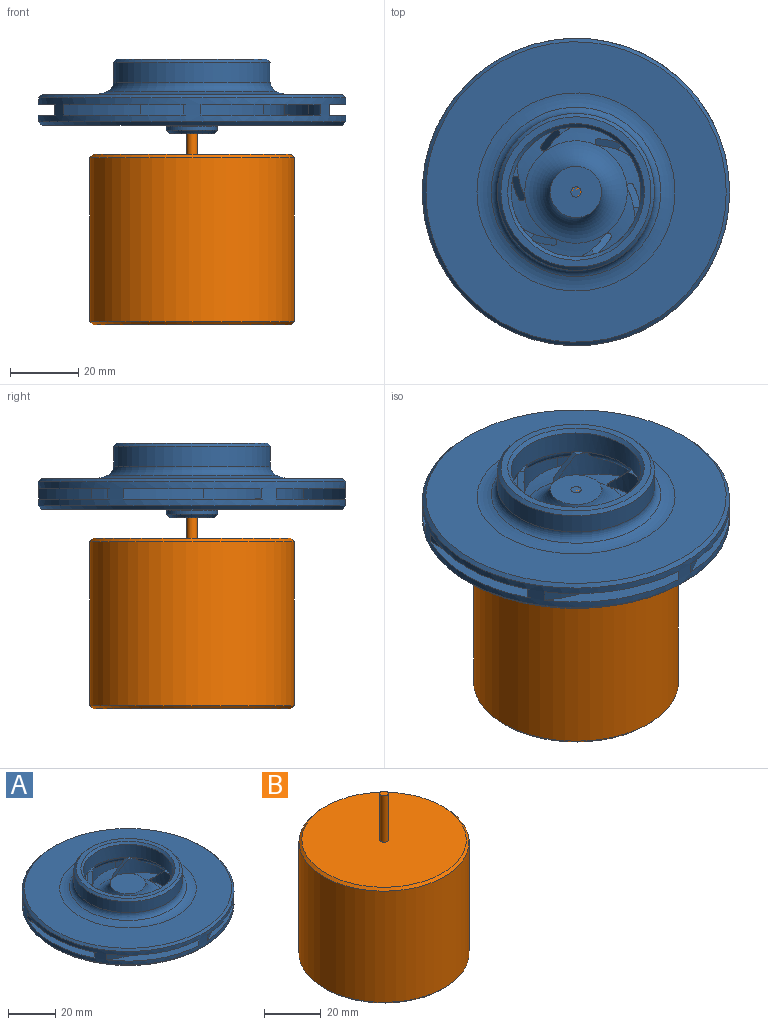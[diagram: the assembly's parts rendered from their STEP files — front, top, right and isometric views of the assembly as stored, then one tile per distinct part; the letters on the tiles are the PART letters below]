
ASSEMBLY  parts=2 mates=1
PART A: 104 faces, bbox 90.1x90.1x22 mm
  f0: plane 58.21x35.73mm, normal (0,0,1), area 534.2mm2, adj f7,f20,f52,f55,f60,f64
  f1: plane 61.99x29.25mm, normal (0,0,1), area 534.2mm2, adj f5,f20,f62,f65,f98,f101
  f2: plane 50.96x43.62mm, normal (0,0,1), area 534.2mm2, adj f6,f20,f53,f56,f70,f73
  f3: plane 61.99x29.25mm, normal (0,0,1), area 534.2mm2, adj f8,f20,f71,f74,f79,f82
  f4: plane 58.21x35.73mm, normal (0,0,1), area 534.2mm2, adj f9,f20,f80,f83,f88,f91
  f5: torus R=29mm, axis (0,0,1), area 246mm2, adj f1,f12,f59,f61,f62,f95,f96,f98
  f6: torus R=29mm, axis (0,0,1), area 246mm2, adj f2,f12,f50,f51,f53,f67,f69,f70
  f7: torus R=29mm, axis (0,0,1), area 246mm2, adj f0,f12,f49,f51,f52,f58,f60,f61
  f8: torus R=29mm, axis (0,0,1), area 246mm2, adj f3,f12,f68,f69,f71,f76,f78,f79
  f9: torus R=29mm, axis (0,0,1), area 246mm2, adj f4,f12,f77,f78,f80,f85,f87,f88
  f10: torus R=29mm, axis (0,0,1), area 246mm2, adj f11,f12,f86,f87,f89,f94,f96,f97
  f11: plane 50.96x43.62mm, normal (0,0,1), area 534.2mm2, adj f10,f20,f89,f92,f97,f100
  f12: torus R=17.12mm, axis (0,0,1), area 718mm2, adj f5,f6,f7,f8,f9,f10,f13
  f13: plane 15x15mm, normal (0,0,1), area 176.7mm2, adj f12
  f14: plane 13x13mm, normal (0,0,-1), area 132.7mm2, adj f103
  f15: cylinder r=7.5mm len=15mm, axis (0,0,1), area 56.8mm2, adj f16,f103
  f16: torus R=10.5mm, axis (0,0,1), area 343.8mm2, adj f15,f17
  f17: torus R=17.12mm, axis (0,0,1), area 226.9mm2, adj f16,f18
  f18: torus R=29mm, axis (0,0,1), area 2006.5mm2, adj f17,f19
  f19: plane 88x88mm, normal (0,0,-1), area 3440mm2, adj f18,f21
  f20: cylinder r=45mm len=90mm, axis (0,0,1), area 1225.1mm2, adj f0,f1,f2,f3,f4,f11,f21,f26
  f21: cone r=45mm half-angle=45deg, axis (0,0,1), area 395.4mm2, adj f19,f20
  f22: torus R=22mm, axis (0,0,1), area 38.9mm2, adj f25,f42,f59,f95,f99
  f23: torus R=22mm, axis (0,0,1), area 38.9mm2, adj f24,f42,f86,f90,f94
  f24: torus R=29mm, axis (0,0,1), area 189.1mm2, adj f23,f26,f86,f89,f94,f97
  f25: torus R=29mm, axis (0,0,1), area 189.1mm2, adj f22,f43,f59,f62,f95,f98
  f26: plane 50.96x43.62mm, normal (0,0,-1), area 534.2mm2, adj f20,f24,f89,f92,f97,f100
  f27: torus R=22mm, axis (0,0,1), area 38.9mm2, adj f28,f42,f77,f81,f85
  f28: torus R=29mm, axis (0,0,1), area 189.1mm2, adj f27,f29,f77,f80,f85,f88
  f29: plane 58.21x35.73mm, normal (0,0,-1), area 534.2mm2, adj f20,f28,f80,f83,f88,f91
  f30: torus R=22mm, axis (0,0,1), area 38.9mm2, adj f31,f42,f68,f72,f76
  f31: torus R=29mm, axis (0,0,1), area 189.1mm2, adj f30,f32,f68,f71,f76,f79
  f32: plane 61.99x29.25mm, normal (0,0,-1), area 534.2mm2, adj f20,f31,f71,f74,f79,f82
  f33: torus R=22mm, axis (0,0,1), area 38.9mm2, adj f34,f42,f50,f54,f67
  f34: torus R=29mm, axis (0,0,1), area 189.1mm2, adj f33,f35,f50,f53,f67,f70
  f35: plane 50.96x43.62mm, normal (0,0,-1), area 534.2mm2, adj f20,f34,f53,f56,f70,f73
  f36: torus R=22mm, axis (0,0,1), area 38.9mm2, adj f37,f42,f49,f58,f63
  f37: torus R=29mm, axis (0,0,1), area 189.1mm2, adj f36,f38,f49,f52,f58,f60
  f38: plane 58.21x35.73mm, normal (0,0,-1), area 534.2mm2, adj f20,f37,f52,f55,f60,f64
  f39: torus R=26mm, axis (0,0,1), area 519.4mm2, adj f40,f45
  f40: cylinder r=23mm len=46mm, axis (0,0,1), area 835.7mm2, adj f39,f47
  f41: plane 44x44mm, normal (0,0,1), area 263.9mm2, adj f47,f48
  f42: cylinder r=19mm len=38mm, axis (0,0,1), area 807.5mm2, adj f22,f23,f27,f30,f33,f36,f48,f57
  f43: plane 61.99x29.25mm, normal (0,0,-1), area 534.2mm2, adj f20,f25,f62,f65,f98,f101
  f44: plane 88x88mm, normal (0,0,1), area 3440mm2, adj f45,f46
  f45: torus R=29mm, axis (0,0,1), area 726mm2, adj f39,f44
  f46: cone r=44mm half-angle=45deg, axis (0,0,-1), area 395.4mm2, adj f20,f44
  f47: cone r=22mm half-angle=45deg, axis (0,0,-1), area 199.9mm2, adj f40,f41
  f48: cone r=19mm half-angle=45deg, axis (0,0,1), area 173.3mm2, adj f41,f42
  f49: cylinder r=19mm len=21.17mm, axis (0,0,1), area 126.5mm2, adj f7,f36,f37,f51,f52,f54,f57
  f50: cylinder r=21mm len=23.4mm, axis (0,0,1), area 116.1mm2, adj f6,f33,f34,f51,f53,f54
  f51: cylinder r=1mm len=1.84mm, axis (0,0,1), area 1.5mm2, adj f6,f7,f49,f50,f54
  f52: cylinder r=34mm len=21.3mm, axis (0,0,1), area 89.6mm2, adj f0,f7,f37,f38,f49,f55
  f53: cylinder r=36mm len=22.55mm, axis (0,0,1), area 92.5mm2, adj f2,f6,f34,f35,f50,f56
  f54: plane 7.34x6.34mm, normal (0.58,0.4,0.71), area 20.1mm2, adj f33,f49,f50,f51,f57
  f55: cylinder r=44mm len=27.23mm, axis (0,0,1), area 83.8mm2, adj f0,f20,f38,f52
  f56: cylinder r=46mm len=23.57mm, axis (0,0,1), area 72.8mm2, adj f2,f20,f35,f53
  f57: plane 3.97x2.02mm, normal (0,0,1), area 3mm2, adj f42,f49,f54
  f58: cylinder r=21mm len=19.33mm, axis (0,0,1), area 116.1mm2, adj f7,f36,f37,f60,f61,f63
  f59: cylinder r=19mm len=17.49mm, axis (0,0,1), area 126.5mm2, adj f5,f22,f25,f61,f62,f63,f66
  f60: cylinder r=36mm len=29.01mm, axis (0,0,1), area 92.5mm2, adj f0,f7,f37,f38,f58,f64
  f61: cylinder r=1mm len=2mm, axis (0,0,1), area 1.5mm2, adj f5,f7,f58,f59,f63
  f62: cylinder r=34mm len=27.4mm, axis (0,0,1), area 89.6mm2, adj f1,f5,f25,f43,f59,f65
  f63: plane 7.61x7.34mm, normal (0.64,-0.3,0.71), area 20.1mm2, adj f36,f58,f59,f61,f66
  f64: cylinder r=46mm len=18.19mm, axis (0,0,1), area 72.8mm2, adj f0,f20,f38,f60
  f65: cylinder r=44mm len=21.76mm, axis (0,0,1), area 83.8mm2, adj f1,f20,f43,f62
  f66: plane 3.29x3.08mm, normal (0,0,1), area 3mm2, adj f42,f59,f63
  f67: cylinder r=19mm len=22.32mm, axis (0,0,1), area 126.5mm2, adj f6,f33,f34,f69,f70,f72,f75
  f68: cylinder r=21mm len=24.67mm, axis (0,0,1), area 116.1mm2, adj f8,f30,f31,f69,f71,f72
  f69: cylinder r=1mm len=1.89mm, axis (0,0,1), area 1.5mm2, adj f6,f8,f67,f68,f72
  f70: cylinder r=34mm len=26.16mm, axis (0,0,1), area 89.6mm2, adj f2,f6,f34,f35,f67,f73
  f71: cylinder r=36mm len=27.7mm, axis (0,0,1), area 92.5mm2, adj f3,f8,f31,f32,f68,f74
  f72: plane 7.34x7.28mm, normal (-0.06,0.7,0.71), area 20.1mm2, adj f30,f67,f68,f69,f75
  f73: cylinder r=44mm len=25.39mm, axis (0,0,1), area 83.8mm2, adj f2,f20,f35,f70
  f74: cylinder r=46mm len=22.63mm, axis (0,0,1), area 72.8mm2, adj f3,f20,f32,f71
  f75: plane 3.8x1.58mm, normal (0,0,1), area 3mm2, adj f42,f67,f72
  f76: cylinder r=19mm len=17.49mm, axis (0,0,1), area 126.5mm2, adj f8,f30,f31,f78,f79,f81,f84
  f77: cylinder r=21mm len=19.33mm, axis (0,0,1), area 116.1mm2, adj f9,f27,f28,f78,f80,f81
  f78: cylinder r=1mm len=2mm, axis (0,0,1), area 1.5mm2, adj f8,f9,f76,f77,f81
  f79: cylinder r=34mm len=27.4mm, axis (0,0,1), area 89.6mm2, adj f3,f8,f31,f32,f76,f82
  f80: cylinder r=36mm len=29.01mm, axis (0,0,1), area 92.5mm2, adj f4,f9,f28,f29,f77,f83
  f81: plane 7.61x7.34mm, normal (-0.64,0.3,0.71), area 20.1mm2, adj f27,f76,f77,f78,f84
  f82: cylinder r=44mm len=21.76mm, axis (0,0,1), area 83.8mm2, adj f3,f20,f32,f79
  f83: cylinder r=46mm len=18.19mm, axis (0,0,1), area 72.8mm2, adj f4,f20,f29,f80
  f84: plane 3.29x3.08mm, normal (0,0,1), area 3mm2, adj f42,f76,f81
  f85: cylinder r=19mm len=21.17mm, axis (0,0,1), area 126.5mm2, adj f9,f27,f28,f87,f88,f90,f93
  f86: cylinder r=21mm len=23.4mm, axis (0,0,1), area 116.1mm2, adj f10,f23,f24,f87,f89,f90
  f87: cylinder r=1mm len=1.84mm, axis (0,0,1), area 1.5mm2, adj f9,f10,f85,f86,f90
  f88: cylinder r=34mm len=21.3mm, axis (0,0,1), area 89.6mm2, adj f4,f9,f28,f29,f85,f91
  f89: cylinder r=36mm len=22.55mm, axis (0,0,1), area 92.5mm2, adj f10,f11,f24,f26,f86,f92
  f90: plane 7.34x6.34mm, normal (-0.58,-0.4,0.71), area 20.1mm2, adj f23,f85,f86,f87,f93
  f91: cylinder r=44mm len=27.23mm, axis (0,0,1), area 83.8mm2, adj f4,f20,f29,f88
  f92: cylinder r=46mm len=23.57mm, axis (0,0,1), area 72.8mm2, adj f11,f20,f26,f89
  f93: plane 3.97x2.02mm, normal (0,0,1), area 3mm2, adj f42,f85,f90
  f94: cylinder r=19mm len=22.32mm, axis (0,0,1), area 126.5mm2, adj f10,f23,f24,f96,f97,f99,f102
  f95: cylinder r=21mm len=24.67mm, axis (0,0,1), area 116.1mm2, adj f5,f22,f25,f96,f98,f99
  f96: cylinder r=1mm len=1.89mm, axis (0,0,1), area 1.5mm2, adj f5,f10,f94,f95,f99
  f97: cylinder r=34mm len=26.16mm, axis (0,0,1), area 89.6mm2, adj f10,f11,f24,f26,f94,f100
  f98: cylinder r=36mm len=27.7mm, axis (0,0,1), area 92.5mm2, adj f1,f5,f25,f43,f95,f101
  f99: plane 7.34x7.28mm, normal (0.06,-0.7,0.71), area 20.1mm2, adj f22,f94,f95,f96,f102
  f100: cylinder r=44mm len=25.39mm, axis (0,0,1), area 83.8mm2, adj f11,f20,f26,f97
  f101: cylinder r=46mm len=22.63mm, axis (0,0,1), area 72.8mm2, adj f1,f20,f43,f98
  f102: plane 3.8x1.58mm, normal (0,0,1), area 3mm2, adj f42,f94,f99
  f103: cone r=7.5mm half-angle=45deg, axis (0,0,1), area 62.2mm2, adj f14,f15
PART B: 318 faces, bbox 60x60x70 mm
  f0: plane 58x58mm, normal (0,0,-1), area 2389.9mm2, adj f5,f7,f8,f9,f10,f11,f12,f13
  f1: cylinder r=30mm len=60mm, axis (0,0,1), area 9047.8mm2, adj f5,f6
  f2: plane 58x58mm, normal (0,0,1), area 2635mm2, adj f3,f6
  f3: cylinder r=1.5mm len=20mm, axis (0,0,1), area 188.5mm2, adj f2,f4
  f4: plane 3x3mm, normal (0,0,1), area 7.1mm2, adj f3
  f5: cone r=30mm half-angle=45deg, axis (0,0,1), area 262.1mm2, adj f0,f1
  f6: cone r=29mm half-angle=45deg, axis (0,0,-1), area 262.1mm2, adj f1,f2
  f7: plane 1x0.85mm, normal (1,-0.05,0), area 0.9mm2, adj f0,f8,f28,f29
  f8: extruded ~1x0.79mm, area 0.8mm2, adj f0,f7,f9,f29
  f9: extruded ~2.7x1mm, area 2.7mm2, adj f0,f8,f10,f29
  f10: extruded ~3.41x2.78mm, area 4.4mm2, adj f0,f9,f11,f29
  f11: extruded ~1.77x1mm, area 1.8mm2, adj f0,f10,f12,f29
  f12: plane 1x0.79mm, normal (1,-0.09,0), area 0.8mm2, adj f0,f11,f13,f29
  f13: extruded ~3.71x1mm, area 3.7mm2, adj f0,f12,f14,f29
  f14: extruded ~1.94x1.2mm, area 2.4mm2, adj f0,f13,f15,f29
  f15: extruded ~3.9x2.28mm, area 5.1mm2, adj f0,f14,f16,f29
  f16: plane 1x0.84mm, normal (-0.98,-0.2,0), area 0.9mm2, adj f0,f15,f17,f29
  f17: extruded ~1.48x1mm, area 1.5mm2, adj f0,f16,f18,f29
  f18: extruded ~1.77x1.51mm, area 2.6mm2, adj f0,f17,f19,f29
  f19: extruded ~1.98x1.95mm, area 3mm2, adj f0,f18,f20,f29
  f20: extruded ~2.61x1mm, area 2.6mm2, adj f0,f19,f21,f29
  f21: plane 1x0.78mm, normal (-1,0,0), area 0.8mm2, adj f0,f20,f22,f29
  f22: extruded ~4.9x1mm, area 4.9mm2, adj f0,f21,f23,f29
  f23: extruded ~3.08x2.53mm, area 4mm2, adj f0,f22,f24,f29
  f24: extruded ~1x0.55mm, area 0.7mm2, adj f0,f23,f25,f29
  f25: plane 1x0.6mm, normal (-0.75,0.66,0), area 0.8mm2, adj f0,f24,f26,f29
  f26: extruded ~1x0.56mm, area 0.6mm2, adj f0,f25,f27,f29
  f27: extruded ~3.17x1mm, area 3.2mm2, adj f0,f26,f28,f29
  f28: extruded ~1x0.82mm, area 0.8mm2, adj f0,f7,f27,f29
  f29: plane 8.49x7.99mm, normal (0,0,-1), area 18.1mm2, adj f7,f8,f9,f10,f11,f12,f13,f14
  f30: extruded ~1x0.69mm, area 0.9mm2, adj f0,f31,f40,f41
  f31: extruded ~3.03x2.59mm, area 4mm2, adj f0,f30,f32,f41
  f32: extruded ~2.06x1mm, area 2.6mm2, adj f0,f31,f33,f41
  f33: extruded ~3.25x2.86mm, area 4.3mm2, adj f0,f32,f34,f41
  f34: extruded ~1x0.75mm, area 1mm2, adj f0,f33,f35,f41
  f35: plane 1x0.75mm, normal (-0.67,-0.74,0), area 1mm2, adj f0,f34,f36,f41
  f36: extruded ~3.85x3.33mm, area 5.1mm2, adj f0,f35,f37,f41
  f37: extruded ~1.25x1mm, area 1.6mm2, adj f0,f36,f38,f41
  f38: extruded ~2.96x2.43mm, area 3.8mm2, adj f0,f37,f39,f41
  f39: extruded ~1x0.71mm, area 0.9mm2, adj f0,f38,f40,f41
  f40: plane 1x0.78mm, normal (-0.66,0.75,0), area 1mm2, adj f0,f30,f39,f41
  f41: plane 8.96x5.52mm, normal (0,0,-1), area 10.7mm2, adj f30,f31,f32,f33,f34,f35,f36,f37
  f42: plane 1x0.76mm, normal (0,-1,0), area 0.8mm2, adj f0,f43,f73,f76
  f43: plane 2.48x1mm, normal (-1,0,0), area 2.5mm2, adj f0,f42,f44,f76
  f44: extruded ~2.47x2.15mm, area 3.3mm2, adj f0,f43,f45,f76
  f45: extruded ~1x0.6mm, area 0.8mm2, adj f0,f44,f46,f76
  f46: extruded ~2.66x2.07mm, area 3.4mm2, adj f0,f45,f47,f76
  f47: plane 2.12x1mm, normal (0,-1,0), area 2.1mm2, adj f0,f46,f48,f76
  f48: plane 2.56x1mm, normal (-1,0,0), area 2.6mm2, adj f0,f47,f49,f76
  f49: plane 2.47x1mm, normal (0,1,0), area 2.5mm2, adj f0,f48,f50,f76
  f50: plane 1x0.87mm, normal (-1,0,0), area 0.9mm2, adj f0,f49,f51,f76
  f51: plane 2.94x1mm, normal (0,-1,0), area 2.9mm2, adj f0,f50,f52,f76
  f52: plane 1x0.67mm, normal (-1,0,0), area 0.7mm2, adj f0,f51,f53,f76
  f53: plane 2.94x1mm, normal (0,1,0), area 2.9mm2, adj f0,f52,f54,f76
  f54: plane 1.06x1mm, normal (-1,0,0), area 1.1mm2, adj f0,f53,f55,f76
  f55: plane 1x0.76mm, normal (0,1,0), area 0.8mm2, adj f0,f54,f56,f76
  f56: plane 1.06x1mm, normal (1,0,0), area 1.1mm2, adj f0,f55,f57,f76
  f57: plane 2.77x1mm, normal (0,1,0), area 2.8mm2, adj f0,f56,f58,f76
  f58: plane 1x0.67mm, normal (1,0,0), area 0.7mm2, adj f0,f57,f59,f76
  f59: plane 2.77x1mm, normal (0,-1,0), area 2.8mm2, adj f0,f58,f60,f76
  f60: plane 1x0.87mm, normal (1,0,0), area 0.9mm2, adj f0,f59,f61,f76
  f61: plane 2.34x1mm, normal (0,1,0), area 2.3mm2, adj f0,f60,f62,f76
  f62: plane 2.56x1mm, normal (1,0,0), area 2.6mm2, adj f0,f61,f63,f76
  f63: plane 1.94x1mm, normal (0,-1,0), area 1.9mm2, adj f0,f62,f64,f76
  f64: extruded ~2.56x2.11mm, area 3.4mm2, adj f0,f63,f65,f76
  f65: extruded ~1x0.58mm, area 0.8mm2, adj f0,f64,f66,f76
  f66: extruded ~2.47x2.21mm, area 3.3mm2, adj f0,f65,f73,f76
  f67: plane 1.63x1mm, normal (0,-1,0), area 1.6mm2, adj f68,f74,f76,f77
  f68: plane 1.32x1mm, normal (1,0,0), area 1.3mm2, adj f67,f69,f76,f77
  f69: plane 1.63x1mm, normal (0,1,0), area 1.6mm2, adj f68,f74,f76,f77
  f70: plane 1.32x1mm, normal (1,0,0), area 1.3mm2, adj f71,f75,f76,f314
  f71: plane 1.72x1mm, normal (0,1,0), area 1.7mm2, adj f70,f72,f76,f314
  f72: plane 1.32x1mm, normal (-1,0,0), area 1.3mm2, adj f71,f75,f76,f314
  f73: plane 2.52x1mm, normal (1,0,0), area 2.5mm2, adj f0,f42,f66,f76
  f74: plane 1.32x1mm, normal (-1,0,0), area 1.3mm2, adj f67,f69,f76,f77
  f75: plane 1.72x1mm, normal (0,-1,0), area 1.7mm2, adj f70,f72,f76,f314
  f76: plane 8.17x6.73mm, normal (0,0,-1), area 22.6mm2, adj f42,f43,f44,f45,f46,f47,f48,f49
  f77: plane 1.63x1.32mm, normal (0,0,-1), area 2.2mm2, adj f67,f68,f69,f74
  f78: plane 2.21x1mm, normal (0,1,0), area 2.2mm2, adj f0,f79,f90,f91
  f79: plane 1x0.73mm, normal (1,0,0), area 0.7mm2, adj f0,f78,f80,f91
  f80: plane 1.45x1mm, normal (0,-1,0), area 1.4mm2, adj f0,f79,f81,f91
  f81: plane 2.64x1mm, normal (1,0,0), area 2.6mm2, adj f0,f80,f82,f91
  f82: extruded ~1.58x1.19mm, area 2mm2, adj f0,f81,f83,f91
  f83: plane 1x0.78mm, normal (0.88,-0.47,0), area 0.9mm2, adj f0,f82,f84,f91
  f84: extruded ~1.57x1.33mm, area 2.1mm2, adj f0,f83,f85,f91
  f85: extruded ~2.95x1.23mm, area 3.3mm2, adj f0,f84,f86,f91
  f86: extruded ~4.42x1mm, area 4.4mm2, adj f0,f85,f87,f91
  f87: extruded ~1x0.79mm, area 0.8mm2, adj f0,f86,f88,f91
  f88: extruded ~4.67x1mm, area 4.7mm2, adj f0,f87,f89,f91
  f89: extruded ~2.59x1.17mm, area 3mm2, adj f0,f88,f90,f91
  f90: plane 3.32x1mm, normal (-1,0,0), area 3.3mm2, adj f0,f78,f89,f91
  f91: plane 9.6x5.33mm, normal (0,0,-1), area 11.1mm2, adj f78,f79,f80,f81,f82,f83,f84,f85
  f92: extruded ~1.81x1.61mm, area 2.4mm2, adj f0,f93,f95,f96
  f93: plane 1x0.57mm, normal (0.63,0.78,0), area 0.7mm2, adj f0,f92,f94,f96
  f94: extruded ~1.77x1.66mm, area 2.4mm2, adj f0,f93,f95,f96
  f95: plane 1x0.62mm, normal (-0.64,-0.77,0), area 0.8mm2, adj f0,f92,f94,f96
  f96: plane 2.39x2.11mm, normal (0,0,-1), area 1.8mm2, adj f92,f93,f94,f95
  f97: extruded ~1x0.69mm, area 0.9mm2, adj f0,f98,f107,f108
  f98: extruded ~3.03x2.59mm, area 4mm2, adj f0,f97,f99,f108
  f99: extruded ~2.06x1mm, area 2.6mm2, adj f0,f98,f100,f108
  f100: extruded ~3.25x2.86mm, area 4.3mm2, adj f0,f99,f101,f108
  f101: extruded ~1x0.75mm, area 1mm2, adj f0,f100,f102,f108
  f102: plane 1x0.75mm, normal (-0.67,-0.74,0), area 1mm2, adj f0,f101,f103,f108
  f103: extruded ~3.85x3.33mm, area 5.1mm2, adj f0,f102,f104,f108
  f104: extruded ~1.25x1mm, area 1.6mm2, adj f0,f103,f105,f108
  f105: extruded ~2.96x2.43mm, area 3.8mm2, adj f0,f104,f106,f108
  f106: extruded ~1x0.71mm, area 0.9mm2, adj f0,f105,f107,f108
  f107: plane 1x0.78mm, normal (-0.66,0.75,0), area 1mm2, adj f0,f97,f106,f108
  f108: plane 8.96x5.52mm, normal (0,0,-1), area 10.7mm2, adj f97,f98,f99,f100,f101,f102,f103,f104
  f109: extruded ~1.44x1mm, area 1.5mm2, adj f0,f110,f116,f117
  f110: extruded ~3.31x1.99mm, area 4.3mm2, adj f0,f109,f111,f117
  f111: extruded ~3.52x1mm, area 3.6mm2, adj f0,f110,f112,f117
  f112: plane 1x0.89mm, normal (-1,0.01,0), area 0.9mm2, adj f0,f111,f113,f117
  f113: extruded ~3.53x1mm, area 3.6mm2, adj f0,f112,f114,f117
  f114: extruded ~2.44x1.32mm, area 3.1mm2, adj f0,f113,f115,f117
  f115: extruded ~1.17x1mm, area 1.2mm2, adj f0,f114,f116,f117
  f116: plane 1x0.84mm, normal (-0.1,1,0), area 0.8mm2, adj f0,f109,f115,f117
  f117: plane 6.83x3.43mm, normal (0,0,-1), area 7.4mm2, adj f109,f110,f111,f112,f113,f114,f115,f116
  f118: plane 1x0.93mm, normal (-0.37,0.93,0), area 1mm2, adj f0,f119,f135,f136
  f119: extruded ~1x0.8mm, area 0.9mm2, adj f0,f118,f120,f136
  f120: extruded ~7.44x3.65mm, area 8.3mm2, adj f0,f119,f121,f136
  f121: plane 1x0.91mm, normal (0.32,-0.95,0), area 1mm2, adj f0,f120,f122,f136
  f122: extruded ~2.34x1mm, area 2.5mm2, adj f0,f121,f123,f136
  f123: extruded ~2x1.65mm, area 2.7mm2, adj f0,f122,f124,f136
  f124: extruded ~1x0.75mm, area 1.2mm2, adj f0,f123,f125,f136
  f125: extruded ~1.96x1mm, area 2mm2, adj f0,f124,f126,f136
  f126: extruded ~1.49x1.31mm, area 2.2mm2, adj f0,f125,f127,f136
  f127: extruded ~2.92x2.82mm, area 4.4mm2, adj f0,f126,f128,f136
  f128: plane 1x0.69mm, normal (-0.63,0.78,0), area 0.9mm2, adj f0,f127,f129,f136
  f129: extruded ~2.51x2.09mm, area 3.5mm2, adj f0,f128,f130,f136
  f130: extruded ~1x0.82mm, area 1.2mm2, adj f0,f129,f131,f136
  f131: extruded ~1.91x1mm, area 1.9mm2, adj f0,f130,f132,f136
  f132: extruded ~1.26x1.22mm, area 2mm2, adj f0,f131,f133,f136
  f133: extruded ~1.51x1mm, area 1.7mm2, adj f0,f132,f134,f136
  f134: extruded ~3.53x1.99mm, area 4.1mm2, adj f0,f133,f135,f136
  f135: extruded ~1x0.5mm, area 0.6mm2, adj f0,f118,f134,f136
  f136: plane 9x8.54mm, normal (0,0,-1), area 16.6mm2, adj f118,f119,f120,f121,f122,f123,f124,f125
  f137: plane 1x0.56mm, normal (0.38,0.93,0), area 0.6mm2, adj f0,f138,f140,f141
  f138: extruded ~1.46x1mm, area 1.7mm2, adj f0,f137,f139,f141
  f139: plane 1x0.56mm, normal (-0.42,-0.91,0), area 0.6mm2, adj f0,f138,f140,f141
  f140: extruded ~1.43x1mm, area 1.7mm2, adj f0,f137,f139,f141
  f141: plane 1.69x1.42mm, normal (0,0,-1), area 1mm2, adj f137,f138,f139,f140
  f142: plane 1x0.55mm, normal (0.4,0.92,0), area 0.6mm2, adj f0,f143,f145,f146
  f143: extruded ~1.44x1mm, area 1.7mm2, adj f0,f142,f144,f146
  f144: plane 1x0.57mm, normal (-0.4,-0.92,0), area 0.6mm2, adj f0,f143,f145,f146
  f145: extruded ~1.43x1mm, area 1.7mm2, adj f0,f142,f144,f146
  f146: plane 1.68x1.44mm, normal (0,0,-1), area 1mm2, adj f142,f143,f144,f145
  f147: extruded ~2.73x1mm, area 2.7mm2, adj f0,f148,f152,f153
  f148: extruded ~2.78x1mm, area 2.8mm2, adj f0,f147,f149,f153
  f149: plane 1x0.85mm, normal (-1,0,0), area 0.9mm2, adj f0,f148,f150,f153
  f150: extruded ~2.78x1mm, area 2.8mm2, adj f0,f149,f151,f153
  f151: extruded ~2.73x1mm, area 2.7mm2, adj f0,f150,f152,f153
  f152: plane 1x0.85mm, normal (1,0,0), area 0.9mm2, adj f0,f147,f151,f153
  f153: plane 5.51x0.98mm, normal (0,0,-1), area 4.6mm2, adj f147,f148,f149,f150,f151,f152
  f154: extruded ~1x0.69mm, area 0.7mm2, adj f0,f155,f176,f177
  f155: plane 2.84x1mm, normal (0,1,0), area 2.8mm2, adj f0,f154,f156,f177
  f156: extruded ~1x0.39mm, area 0.4mm2, adj f0,f155,f157,f177
  f157: extruded ~1x0.82mm, area 0.9mm2, adj f0,f156,f158,f177
  f158: plane 1x0.94mm, normal (-0.31,0.95,0), area 1mm2, adj f0,f157,f159,f177
  f159: extruded ~1x0.83mm, area 0.9mm2, adj f0,f158,f160,f177
  f160: extruded ~3.61x3.34mm, area 5mm2, adj f0,f159,f161,f177
  f161: plane 1x0.7mm, normal (0.61,-0.79,0), area 0.9mm2, adj f0,f160,f162,f177
  f162: extruded ~2.76x2.74mm, area 3.9mm2, adj f0,f161,f163,f177
  f163: plane 3.54x1mm, normal (0,-1,0), area 3.5mm2, adj f0,f162,f164,f177
  f164: extruded ~2.78x1.34mm, area 3.1mm2, adj f0,f163,f165,f177
  f165: extruded ~2.29x1.3mm, area 2.6mm2, adj f0,f164,f166,f177
  f166: plane 1x0.61mm, normal (0.76,0.65,0), area 0.8mm2, adj f0,f165,f167,f177
  f167: extruded ~2.28x1.38mm, area 2.7mm2, adj f0,f166,f168,f177
  f168: extruded ~4.11x2.59mm, area 4.9mm2, adj f0,f167,f169,f177
  f169: plane 1x0.75mm, normal (0.65,-0.76,0), area 1mm2, adj f0,f168,f170,f177
  f170: extruded ~4.08x2.77mm, area 5mm2, adj f0,f169,f171,f177
  f171: extruded ~1x0.99mm, area 1.2mm2, adj f0,f170,f172,f177
  f172: plane 1x0.75mm, normal (-0.79,-0.61,0), area 0.9mm2, adj f0,f171,f173,f177
  f173: extruded ~1.01x1mm, area 1.2mm2, adj f0,f172,f174,f177
  f174: extruded ~3.09x1.52mm, area 3.5mm2, adj f0,f173,f175,f177
  f175: extruded ~1x0.56mm, area 0.6mm2, adj f0,f174,f176,f177
  f176: plane 1x0.68mm, normal (-0.52,0.85,0), area 0.8mm2, adj f0,f154,f175,f177
  f177: plane 8.96x8.15mm, normal (0,0,-1), area 19.4mm2, adj f154,f155,f156,f157,f158,f159,f160,f161
  f178: extruded ~3x1.6mm, area 3.4mm2, adj f0,f179,f214,f216
  f179: extruded ~1.56x1mm, area 1.6mm2, adj f0,f178,f180,f216
  f180: extruded ~2.86x1mm, area 2.9mm2, adj f0,f179,f181,f216
  f181: plane 1x0.78mm, normal (-1,0.01,0), area 0.8mm2, adj f0,f180,f182,f216
  f182: extruded ~2.86x1mm, area 2.9mm2, adj f0,f181,f183,f216
  f183: plane 1.48x1mm, normal (-1,0,0), area 1.5mm2, adj f0,f182,f184,f216
  f184: extruded ~2.67x1mm, area 2.7mm2, adj f0,f183,f185,f216
  f185: plane 1x0.76mm, normal (-1,0.01,0), area 0.8mm2, adj f0,f184,f186,f216
  f186: extruded ~2.65x1mm, area 2.7mm2, adj f0,f185,f187,f216
  f187: extruded ~1x0.57mm, area 0.6mm2, adj f0,f186,f188,f216
  f188: extruded ~1x0.69mm, area 0.7mm2, adj f0,f187,f189,f216
  f189: plane 1x0.89mm, normal (0,1,0), area 0.9mm2, adj f0,f188,f190,f216
  f190: extruded ~1x0.61mm, area 0.6mm2, adj f0,f189,f191,f216
  f191: plane 1x0.68mm, normal (1,0,0), area 0.7mm2, adj f0,f190,f192,f216
  f192: plane 1x0.53mm, normal (0,1,0), area 0.5mm2, adj f0,f191,f193,f216
  f193: extruded ~2.42x1mm, area 2.4mm2, adj f0,f192,f194,f216
  f194: plane 1x0.77mm, normal (1,0,0), area 0.8mm2, adj f0,f193,f195,f216
  f195: extruded ~2.43x1mm, area 2.4mm2, adj f0,f194,f196,f216
  f196: plane 1x0.51mm, normal (0,-1,0), area 0.5mm2, adj f0,f195,f197,f216
  f197: plane 1.48x1mm, normal (1,0,0), area 1.5mm2, adj f0,f196,f198,f216
  f198: plane 1x0.55mm, normal (0,1,0), area 0.6mm2, adj f0,f197,f199,f216
  f199: extruded ~2.59x1mm, area 2.6mm2, adj f0,f198,f200,f216
  f200: plane 1x0.79mm, normal (1,0,0), area 0.8mm2, adj f0,f199,f201,f216
  f201: extruded ~2.59x1mm, area 2.6mm2, adj f0,f200,f202,f216
  f202: plane 1x0.57mm, normal (0,-1,0), area 0.6mm2, adj f0,f201,f203,f216
  f203: extruded ~1.38x1mm, area 1.4mm2, adj f0,f202,f204,f216
  f204: extruded ~1x0.86mm, area 0.9mm2, adj f0,f203,f205,f216
  f205: extruded ~2.4x1.57mm, area 3.2mm2, adj f0,f204,f206,f216
  f206: extruded ~2.3x1.53mm, area 3.1mm2, adj f0,f205,f207,f216
  f207: extruded ~1.82x1.45mm, area 2.6mm2, adj f0,f206,f208,f216
  f208: extruded ~1x0.64mm, area 0.6mm2, adj f0,f207,f209,f216
  f209: extruded ~2.49x1.55mm, area 3mm2, adj f0,f208,f214,f216
  f210: extruded ~1.09x1mm, area 1.6mm2, adj f211,f215,f216,f315
  f211: extruded ~1.43x1mm, area 1.8mm2, adj f210,f212,f216,f315
  f212: extruded ~1.51x1mm, area 1.9mm2, adj f211,f213,f216,f315
  f213: extruded ~1x1mm, area 1mm2, adj f212,f215,f216,f315
  f214: plane 1x0.73mm, normal (-0.84,-0.54,0), area 0.9mm2, adj f0,f178,f209,f216
  f215: extruded ~1x0.7mm, area 0.7mm2, adj f210,f213,f216,f315
  f216: plane 8.66x7.06mm, normal (0,0,-1), area 22.9mm2, adj f178,f179,f180,f181,f182,f183,f184,f185
  f217: extruded ~3.94x3.89mm, area 6.1mm2, adj f0,f218,f229,f231
  f218: extruded ~3.96x3.79mm, area 6.1mm2, adj f0,f217,f219,f231
  f219: extruded ~4.52x4.2mm, area 6.8mm2, adj f0,f218,f220,f231
  f220: extruded ~2.76x1.84mm, area 3.7mm2, adj f0,f219,f221,f231
  f221: extruded ~3.21x2.42mm, area 4.3mm2, adj f0,f220,f222,f231
  f222: extruded ~2.97x1mm, area 3mm2, adj f0,f221,f223,f231
  f223: extruded ~2.99x2.74mm, area 4.5mm2, adj f0,f222,f224,f231
  f224: extruded ~3.05x2.62mm, area 4.4mm2, adj f0,f223,f225,f231
  f225: extruded ~1x0.89mm, area 0.9mm2, adj f0,f224,f229,f231
  f226: extruded ~1.88x1.05mm, area 2.3mm2, adj f227,f230,f231,f316
  f227: extruded ~3.33x3.19mm, area 5mm2, adj f226,f228,f231,f316
  f228: extruded ~2.78x1mm, area 2.8mm2, adj f227,f230,f231,f316
  f229: plane 1x0.78mm, normal (0.85,-0.52,0), area 0.9mm2, adj f0,f217,f225,f231
  f230: extruded ~2.43x1.56mm, area 3mm2, adj f226,f228,f231,f316
  f231: plane 8.48x7.73mm, normal (0,0,-1), area 22.4mm2, adj f217,f218,f219,f220,f221,f222,f223,f224
  f232: extruded ~3.03x1mm, area 3mm2, adj f0,f233,f257,f259
  f233: plane 1x0.78mm, normal (-1,-0.01,0), area 0.8mm2, adj f0,f232,f234,f259
  f234: extruded ~3.02x1mm, area 3mm2, adj f0,f233,f235,f259
  f235: plane 1x0.16mm, normal (0,1,0), area 0.2mm2, adj f0,f234,f236,f259
  f236: extruded ~1x0.67mm, area 0.7mm2, adj f0,f235,f237,f259
  f237: plane 1x0.65mm, normal (-1,-0.08,0), area 0.6mm2, adj f0,f236,f238,f259
  f238: plane 1x0.95mm, normal (0,1,0), area 0.9mm2, adj f0,f237,f239,f259
  f239: extruded ~1x0.65mm, area 0.6mm2, adj f0,f238,f240,f259
  f240: extruded ~1x0.68mm, area 0.7mm2, adj f0,f239,f241,f259
  f241: extruded ~4.61x1mm, area 4.6mm2, adj f0,f240,f242,f259
  f242: plane 1x0.81mm, normal (1,-0.03,0), area 0.8mm2, adj f0,f241,f243,f259
  f243: extruded ~4.6x1mm, area 4.6mm2, adj f0,f242,f244,f259
  f244: extruded ~1.02x1mm, area 1mm2, adj f0,f243,f245,f259
  f245: extruded ~1x0.69mm, area 0.7mm2, adj f0,f244,f246,f259
  f246: extruded ~1.82x1.8mm, area 2.8mm2, adj f0,f245,f247,f259
  f247: extruded ~1.73x1.71mm, area 2.7mm2, adj f0,f246,f248,f259
  f248: extruded ~1x0.89mm, area 0.9mm2, adj f0,f247,f249,f259
  f249: extruded ~2.74x1.79mm, area 3.4mm2, adj f0,f248,f250,f259
  f250: plane 1x0.72mm, normal (0.7,-0.72,0), area 1mm2, adj f0,f249,f251,f259
  f251: extruded ~3.67x3.07mm, area 5.2mm2, adj f0,f250,f252,f259
  f252: extruded ~1.32x1mm, area 1.4mm2, adj f0,f251,f253,f259
  f253: extruded ~1.69x1mm, area 1.7mm2, adj f0,f252,f257,f259
  f254: extruded ~1.05x1.02mm, area 1.6mm2, adj f255,f258,f259,f317
  f255: extruded ~1.08x1.04mm, area 1.7mm2, adj f254,f256,f259,f317
  f256: extruded ~1x0.92mm, area 1.2mm2, adj f255,f258,f259,f317
  f257: plane 1x0.14mm, normal (0,-1,0), area 0.1mm2, adj f0,f232,f253,f259
  f258: extruded ~1.47x1mm, area 2mm2, adj f254,f256,f259,f317
  f259: plane 8.73x8.59mm, normal (0,0,-1), area 18.8mm2, adj f232,f233,f234,f235,f236,f237,f238,f239
  f260: extruded ~1.45x1mm, area 1.4mm2, adj f0,f261,f267,f268
  f261: plane 5.72x1mm, normal (0,-1,0), area 5.7mm2, adj f0,f260,f262,f268
  f262: extruded ~1.12x1mm, area 1.1mm2, adj f0,f261,f263,f268
  f263: plane 1.02x1mm, normal (-1,0,0), area 1mm2, adj f0,f262,f264,f268
  f264: extruded ~1.12x1mm, area 1.1mm2, adj f0,f263,f265,f268
  f265: plane 5.71x1mm, normal (0,1,0), area 5.7mm2, adj f0,f264,f266,f268
  f266: extruded ~1.45x1mm, area 1.4mm2, adj f0,f265,f267,f268
  f267: plane 1.02x1mm, normal (1,0,0), area 1mm2, adj f0,f260,f266,f268
  f268: plane 8.28x1.02mm, normal (0,0,-1), area 7.7mm2, adj f260,f261,f262,f263,f264,f265,f266,f267
  f269: extruded ~1x0.84mm, area 0.8mm2, adj f0,f270,f296,f297
  f270: plane 1x0.85mm, normal (-1,0,0), area 0.9mm2, adj f0,f269,f271,f297
  f271: extruded ~1x0.86mm, area 0.9mm2, adj f0,f270,f272,f297
  f272: plane 3.51x1mm, normal (0,1,0), area 3.5mm2, adj f0,f271,f273,f297
  f273: plane 2.21x1mm, normal (-1,0,0), area 2.2mm2, adj f0,f272,f274,f297
  f274: plane 2.71x1mm, normal (0,-1,0), area 2.7mm2, adj f0,f273,f275,f297
  f275: extruded ~1x0.85mm, area 0.9mm2, adj f0,f274,f276,f297
  f276: plane 1x0.83mm, normal (-1,0,0), area 0.8mm2, adj f0,f275,f277,f297
  f277: extruded ~1x0.85mm, area 0.9mm2, adj f0,f276,f278,f297
  f278: plane 4.96x1mm, normal (0,1,0), area 5mm2, adj f0,f277,f279,f297
  f279: extruded ~1x0.94mm, area 0.9mm2, adj f0,f278,f280,f297
  f280: plane 1x0.83mm, normal (1,0,0), area 0.8mm2, adj f0,f279,f281,f297
  f281: extruded ~1x0.94mm, area 0.9mm2, adj f0,f280,f282,f297
  f282: plane 1.39x1mm, normal (0,-1,0), area 1.4mm2, adj f0,f281,f283,f297
  f283: plane 2.21x1mm, normal (1,0,0), area 2.2mm2, adj f0,f282,f284,f297
  f284: plane 2.02x1mm, normal (0,1,0), area 2mm2, adj f0,f283,f285,f297
  f285: extruded ~1x0.99mm, area 1mm2, adj f0,f284,f286,f297
  f286: plane 1x0.87mm, normal (1,0,0), area 0.9mm2, adj f0,f285,f287,f297
  f287: extruded ~1x0.99mm, area 1mm2, adj f0,f286,f288,f297
  f288: plane 2.02x1mm, normal (0,-1,0), area 2mm2, adj f0,f287,f289,f297
  f289: plane 2.35x1mm, normal (1,0,0), area 2.4mm2, adj f0,f288,f290,f297
  f290: extruded ~2.06x1.41mm, area 2.9mm2, adj f0,f289,f291,f297
  f291: extruded ~2.81x1mm, area 2.8mm2, adj f0,f290,f292,f297
  f292: plane 1x0.88mm, normal (-1,-0.06,0), area 0.9mm2, adj f0,f291,f293,f297
  f293: extruded ~2.74x1mm, area 2.7mm2, adj f0,f292,f294,f297
  f294: extruded ~1.32x1mm, area 1.8mm2, adj f0,f293,f295,f297
  f295: plane 2.09x1mm, normal (-1,0,0), area 2.1mm2, adj f0,f294,f296,f297
  f296: plane 3.53x1mm, normal (0,-1,0), area 3.5mm2, adj f0,f269,f295,f297
  f297: plane 8.25x7.55mm, normal (0,0,-1), area 19.9mm2, adj f269,f270,f271,f272,f273,f274,f275,f276
  f298: plane 1x0.81mm, normal (0.33,0.94,0), area 0.9mm2, adj f0,f299,f301,f302
  f299: extruded ~5.1x1.78mm, area 5.5mm2, adj f0,f298,f300,f302
  f300: plane 1x0.84mm, normal (-0.37,-0.93,0), area 0.9mm2, adj f0,f299,f301,f302
  f301: extruded ~5.05x1.81mm, area 5.4mm2, adj f0,f298,f300,f302
  f302: plane 5.39x2.62mm, normal (0,0,-1), area 4.7mm2, adj f298,f299,f300,f301
  f303: plane 1x1mm, normal (-0.02,1,0), area 1mm2, adj f0,f304,f312,f313
  f304: extruded ~1x0.92mm, area 0.9mm2, adj f0,f303,f305,f313
  f305: extruded ~2.75x1mm, area 2.8mm2, adj f0,f304,f306,f313
  f306: extruded ~3.65x2.19mm, area 4.6mm2, adj f0,f305,f307,f313
  f307: extruded ~2.34x1.96mm, area 3.2mm2, adj f0,f306,f308,f313
  f308: plane 1x0.75mm, normal (-0.75,0.66,0), area 1mm2, adj f0,f307,f309,f313
  f309: extruded ~2.1x1.28mm, area 2.6mm2, adj f0,f308,f310,f313
  f310: extruded ~2.86x1.4mm, area 3.4mm2, adj f0,f309,f311,f313
  f311: extruded ~2.44x1mm, area 2.4mm2, adj f0,f310,f312,f313
  f312: extruded ~1x1mm, area 1mm2, adj f0,f303,f311,f313
  f313: plane 7.31x4.32mm, normal (0,0,-1), area 9.1mm2, adj f303,f304,f305,f306,f307,f308,f309,f310
  f314: plane 1.72x1.32mm, normal (0,0,-1), area 2.3mm2, adj f70,f71,f72,f75
  f315: plane 2.52x1.68mm, normal (0,0,-1), area 3.6mm2, adj f210,f211,f212,f213,f215
  f316: plane 5.21x3.19mm, normal (0,0,-1), area 10.2mm2, adj f226,f227,f228,f230
  f317: plane 2.1x2.05mm, normal (0,0,-1), area 3.3mm2, adj f254,f255,f256,f258
PLACE A rot(axis=(0,0,1),180deg) t=(0,0,3)mm
PLACE B at identity fixed
MATE revolute B.f6 <-> A.f12  axis (0,0,1) through (0,0,10)mm
